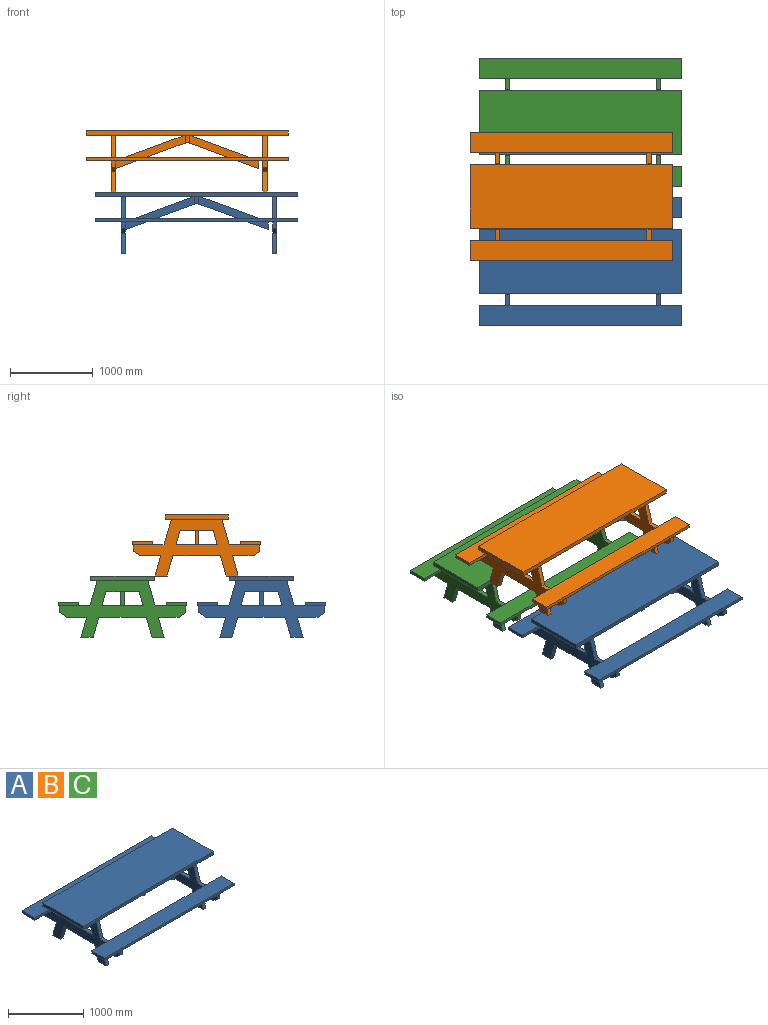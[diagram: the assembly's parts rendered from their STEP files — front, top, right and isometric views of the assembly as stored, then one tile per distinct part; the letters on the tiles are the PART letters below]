
ASSEMBLY  parts=3 mates=1
PART A: 82 faces, bbox 2438.4x1549.4x736.6 mm
  f0: plane 285.75x88.9mm, normal (1,0,0), area 25403.2mm2, adj f27,f67,f69,f80
  f1: plane 285.75x88.9mm, normal (-1,0,0), area 25403.2mm2, adj f27,f67,f69,f74
  f2: plane 1524x685.8mm, normal (1,0,0), area 407111.8mm2, adj f4,f27,f33,f34,f35,f36,f37,f38
  f3: plane 139.96x50.8mm, normal (0,0,1), area 7109.9mm2, adj f20,f25,f26,f61
  f4: plane 139.96x50.8mm, normal (0,0,1), area 7109.9mm2, adj f2,f51,f53,f61
  f5: plane 80.56x50.8mm, normal (0,-1,0), area 4092.2mm2, adj f6,f25,f26,f60
  f6: plane 79.65x53.89mm, normal (0,-0.56,-0.83), area 4885.2mm2, adj f5,f7,f25,f26
  f7: plane 250.39x50.8mm, normal (0,0,-1), area 12720mm2, adj f6,f8,f25,f26
  f8: plane 241.94x69.31mm, normal (0,-0.96,0.28), area 12784.8mm2, adj f7,f9,f25,f26
  f9: plane 145.32x50.8mm, normal (0,0,-1), area 7382.2mm2, adj f8,f10,f25,f26
  f10: plane 241.94x69.31mm, normal (0,0.96,-0.28), area 12784.8mm2, adj f9,f11,f25,f26
  f11: plane 573.28x50.8mm, normal (0,0,-1), area 29122.5mm2, adj f10,f12,f25,f26
  f12: plane 241.94x69.31mm, normal (0,-0.96,-0.28), area 12784.8mm2, adj f11,f13,f25,f26
  f13: plane 145.32x50.8mm, normal (0,0,-1), area 7382.2mm2, adj f12,f14,f25,f26
  f14: plane 241.94x69.31mm, normal (0,0.96,0.28), area 12784.8mm2, adj f13,f15,f25,f26
  f15: plane 244.61x50.8mm, normal (0,0,-1), area 12426mm2, adj f14,f16,f25,f26
  f16: plane 85.44x56.68mm, normal (0,0.55,-0.83), area 5208.3mm2, adj f15,f17,f25,f26
  f17: plane 77.77x50.8mm, normal (0,1,0), area 3950.6mm2, adj f16,f25,f26,f54
  f18: plane 139.96x50.8mm, normal (0,0,1), area 7109.9mm2, adj f19,f25,f26,f57
  f19: plane 309.42x88.64mm, normal (0,0.96,0.28), area 16350.7mm2, adj f18,f25,f26,f27
  f20: plane 309.42x88.64mm, normal (0,-0.96,0.28), area 16350.7mm2, adj f3,f25,f26,f27
  f21: plane 399x50.8mm, normal (0,0,-1), area 20269.4mm2, adj f22,f24,f25,f26
  f22: plane 169.72x50.8mm, normal (0,-0.96,-0.28), area 8968.5mm2, adj f21,f23,f25,f26
  f23: plane 496.25x50.8mm, normal (0,0,1), area 25209.2mm2, adj f22,f24,f25,f26
  f24: plane 169.72x50.8mm, normal (0,0.96,-0.28), area 8968.5mm2, adj f21,f23,f25,f26
  f25: plane 1524x685.8mm, normal (-1,0,0), area 410722.3mm2, adj f3,f5,f6,f7,f8,f9,f10,f11
  f26: plane 1524x685.8mm, normal (1,0,0), area 410722.3mm2, adj f3,f5,f6,f7,f8,f9,f10,f11
  f27: plane 2438.4x762mm, normal (0,0,-1), area 1765157.8mm2, adj f0,f1,f2,f19,f20,f25,f26,f28
  f28: plane 762x50.8mm, normal (-1,0,0), area 38709.6mm2, adj f27,f29,f31,f32
  f29: plane 2438.4x50.8mm, normal (0,-1,0), area 123870.7mm2, adj f27,f28,f30,f32
  f30: plane 762x50.8mm, normal (1,0,0), area 38709.6mm2, adj f27,f29,f31,f32
  f31: plane 2438.4x50.8mm, normal (0,1,0), area 123870.7mm2, adj f27,f28,f30,f32
  f32: plane 2438.4x762mm, normal (0,0,1), area 1858060.8mm2, adj f28,f29,f30,f31
  f33: plane 399x50.8mm, normal (0,0,-1), area 20269.4mm2, adj f2,f34,f52,f53
  f34: plane 169.72x50.8mm, normal (0,-0.96,-0.28), area 8968.5mm2, adj f2,f33,f35,f53
  f35: plane 496.25x50.8mm, normal (0,0,1), area 25209.2mm2, adj f2,f34,f52,f53,f72
  f36: plane 80.56x50.8mm, normal (0,-1,0), area 4092.2mm2, adj f2,f37,f53,f60
  f37: plane 79.65x53.89mm, normal (0,-0.56,-0.83), area 4885.2mm2, adj f2,f36,f38,f53
  f38: plane 250.39x50.8mm, normal (0,0,-1), area 12720mm2, adj f2,f37,f39,f53
  f39: plane 241.94x69.31mm, normal (0,-0.96,0.28), area 12784.8mm2, adj f2,f38,f40,f53
  f40: plane 145.32x50.8mm, normal (0,0,-1), area 7382.2mm2, adj f2,f39,f41,f53
  f41: plane 241.94x69.31mm, normal (0,0.96,-0.28), area 12784.8mm2, adj f2,f40,f42,f53
  f42: plane 573.28x50.8mm, normal (0,0,-1), area 29122.5mm2, adj f2,f41,f43,f53
  f43: plane 241.94x69.31mm, normal (0,-0.96,-0.28), area 12784.8mm2, adj f2,f42,f44,f53
  f44: plane 145.32x50.8mm, normal (0,0,-1), area 7382.2mm2, adj f2,f43,f45,f53
  f45: plane 241.94x69.31mm, normal (0,0.96,0.28), area 12784.8mm2, adj f2,f44,f46,f53
  f46: plane 244.61x50.8mm, normal (0,0,-1), area 12426mm2, adj f2,f45,f47,f53
  f47: plane 85.44x56.68mm, normal (0,0.55,-0.83), area 5208.3mm2, adj f2,f46,f48,f53
  f48: plane 77.77x50.8mm, normal (0,1,0), area 3950.6mm2, adj f2,f47,f53,f54
  f49: plane 139.96x50.8mm, normal (0,0,1), area 7109.9mm2, adj f2,f50,f53,f57
  f50: plane 309.42x88.64mm, normal (0,0.96,0.28), area 16350.7mm2, adj f2,f27,f49,f53
  f51: plane 309.42x88.64mm, normal (0,-0.96,0.28), area 16350.7mm2, adj f2,f4,f27,f53
  f52: plane 169.72x50.8mm, normal (0,0.96,-0.28), area 8968.5mm2, adj f2,f33,f35,f53
  f53: plane 1524x685.8mm, normal (-1,0,0), area 410722.3mm2, adj f4,f27,f33,f34,f35,f36,f37,f38
  f54: plane 2438.4x241.3mm, normal (0,0,-1), area 565160.2mm2, adj f2,f17,f25,f26,f48,f53,f55,f57
  f55: plane 2438.4x38.1mm, normal (0,1,0), area 92903mm2, adj f54,f56,f58,f59
  f56: plane 2438.4x241.3mm, normal (0,0,1), area 588385.9mm2, adj f55,f57,f58,f59
  f57: plane 2438.4x38.1mm, normal (0,-1,0), area 92903mm2, adj f18,f49,f54,f56,f58,f59
  f58: plane 241.3x38.1mm, normal (1,0,0), area 9193.5mm2, adj f54,f55,f56,f57
  f59: plane 241.3x38.1mm, normal (-1,0,0), area 9193.5mm2, adj f54,f55,f56,f57
  f60: plane 2438.4x241.3mm, normal (0,0,-1), area 565160.2mm2, adj f2,f5,f25,f26,f36,f53,f61,f63
  f61: plane 2438.4x38.1mm, normal (0,1,0), area 92903mm2, adj f3,f4,f60,f62,f64,f65
  f62: plane 2438.4x241.3mm, normal (0,0,1), area 588385.9mm2, adj f61,f63,f64,f65
  f63: plane 2438.4x38.1mm, normal (0,-1,0), area 92903mm2, adj f60,f62,f64,f65
  f64: plane 241.3x38.1mm, normal (1,0,0), area 9193.5mm2, adj f60,f61,f62,f63
  f65: plane 241.3x38.1mm, normal (-1,0,0), area 9193.5mm2, adj f60,f61,f62,f63
  f66: plane 285.75x88.9mm, normal (-1,0,0), area 25403.2mm2, adj f27,f67,f70,f75
  f67: plane 609.6x50.8mm, normal (0,0,-1), area 30967.7mm2, adj f0,f1,f66,f68,f69,f70,f71,f76
  f68: plane 285.75x88.9mm, normal (1,0,0), area 25403.2mm2, adj f27,f67,f70,f81
  f69: plane 88.9x50.8mm, normal (0,-1,0), area 4516.1mm2, adj f0,f1,f27,f67
  f70: plane 88.9x50.8mm, normal (0,1,0), area 4516.1mm2, adj f27,f66,f67,f68
  f71: plane 38.1x5.86mm, normal (1,0,0), area 223.4mm2, adj f67,f73,f74,f75
  f72: plane 838.2x309.42mm, normal (-0.35,0,0.94), area 34041.8mm2, adj f27,f35,f74,f75
  f73: plane 838.2x309.42mm, normal (0.35,0,-0.94), area 34041.8mm2, adj f2,f71,f74,f75
  f74: plane 838.2x404.18mm, normal (0,-1,0), area 79431mm2, adj f1,f2,f71,f72,f73
  f75: plane 838.2x404.18mm, normal (0,1,0), area 79431mm2, adj f2,f66,f71,f72,f73
  f76: plane 38.1x5.86mm, normal (-1,0,0), area 223.4mm2, adj f67,f77,f80,f81
  f77: plane 838.2x309.42mm, normal (-0.35,0,-0.94), area 34041.8mm2, adj f76,f78,f80,f81
  f78: plane 94.76x38.1mm, normal (1,0,0), area 3610.5mm2, adj f77,f79,f80,f81
  f79: plane 838.2x309.42mm, normal (0.35,0,0.94), area 34041.8mm2, adj f27,f78,f80,f81
  f80: plane 838.2x404.18mm, normal (0,-1,0), area 79431mm2, adj f0,f76,f77,f78,f79
  f81: plane 838.2x404.18mm, normal (0,1,0), area 79431mm2, adj f68,f76,f77,f78,f79
PART B: same geometry as A
PART C: same geometry as A
PLACE A at identity
PLACE B t=(-116.84,782.4,736.6)mm
PLACE C t=(0,1676.4,0)mm
MATE planar B.f9 <-> A.f32  axis (0,0,-1) through (2042.16,734.79,50.8)mm
